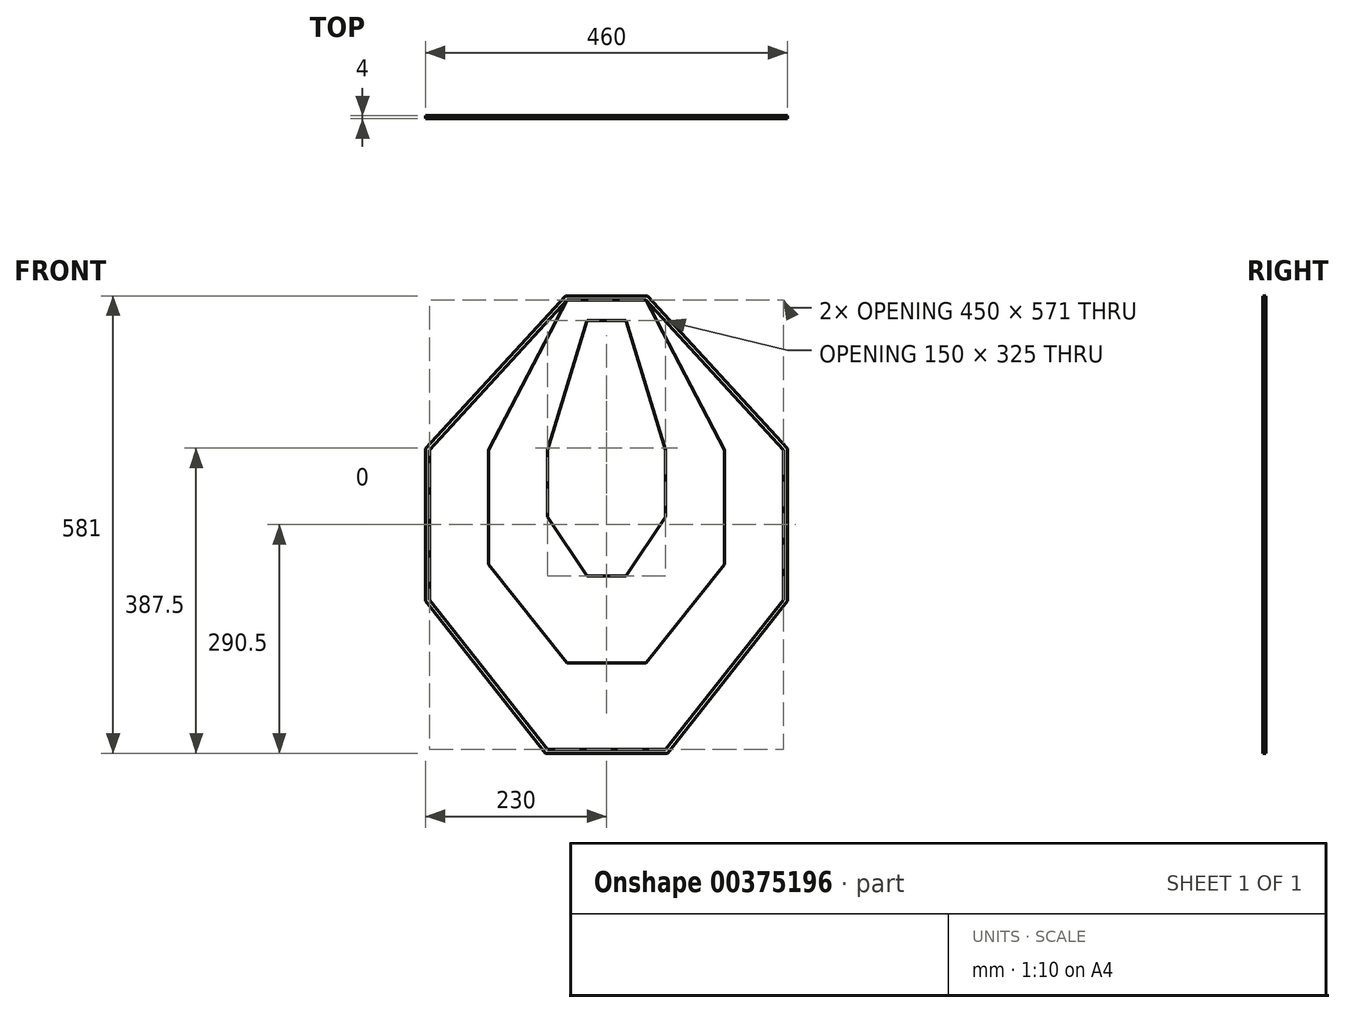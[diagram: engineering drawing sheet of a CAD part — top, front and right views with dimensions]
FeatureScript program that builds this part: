
annotation { "Feature Type Name" : "Feature", "Feature Type Description" : "" }
export const myFeature = defineFeature(function(context is Context, id is Id, definition is map)
    precondition{}
    {
        {
            var Q0;
            Q0=qCreatedBy(makeId("Front.planeOp"),FACE);
            var sketch = newSketch(context, id + "F0", { "sketchPlane" : qUnion([Q0])});
            skLineSegment(sketch, "E0", {"start": v(-25, -26) * mm, "end": v(25, -26) * mm});
            skLineSegment(sketch, "E1", {"start": v(25, -26) * mm, "end": v(75, -191) * mm});
            skLineSegment(sketch, "E2", {"start": v(75, -191) * mm, "end": v(75, -276) * mm});
            skLineSegment(sketch, "E3", {"start": v(75, -276) * mm, "end": v(25, -351) * mm});
            skLineSegment(sketch, "E4", {"start": v(25, -351) * mm, "end": v(-25, -351) * mm});
            skLineSegment(sketch, "E5", {"start": v(-25, -351) * mm, "end": v(-75, -276) * mm});
            skLineSegment(sketch, "E6", {"start": v(-75, -276) * mm, "end": v(-75, -191) * mm});
            skLineSegment(sketch, "E7", {"start": v(-75, -191) * mm, "end": v(-25, -26) * mm});
            skLineSegment(sketch, "E8", {"start": v(0, -26) * mm, "end": v(0, -191) * mm, "construction": true});
            skLineSegment(sketch, "E9", {"start": v(0, -191) * mm, "end": v(0, -351) * mm, "construction": true});
            skLineSegment(sketch, "E10", {"start": v(75, -191) * mm, "end": v(0, -191) * mm, "construction": true});
            skLineSegment(sketch, "E11", {"start": v(-75, -191) * mm, "end": v(0, -191) * mm, "construction": true});
            skLineSegment(sketch, "E12", {"start": v(0, 0) * mm, "end": v(0, -26) * mm, "construction": true});
            skSolve(sketch);
        }
        {
            var Q0;
            Q0=makeQuery(id+"F0.imprint","IMPRINT",FACE,{"disambiguationData":[TD([[makeQuery(id+"F0.imprint","IMPRINT",EDGE,{"derivedFrom":sQuery(id+"F0.wireOp",EDGE,"E0")}),-1.0]])]});
            extrude(context, id + "F1", {"entities" : qUnion([Q0]), "oppositeDirection" : true, "depth" : 3 * mm});
        }
        {
            var Q0;
            Q0=qCreatedBy(makeId("Front.planeOp"),FACE);
            var sketch = newSketch(context, id + "F2", { "sketchPlane" : qUnion([Q0])});
            skLineSegment(sketch, "E13.0", {"start": v(-75, -191) * mm, "end": v(-25, -26) * mm});
            skLineSegment(sketch, "E14.0", {"start": v(-25, -26) * mm, "end": v(25, -26) * mm});
            skLineSegment(sketch, "E15.0", {"start": v(25, -26) * mm, "end": v(75, -191) * mm});
            skLineSegment(sketch, "E16.0", {"start": v(75, -191) * mm, "end": v(75, -276) * mm});
            skLineSegment(sketch, "E17.0", {"start": v(75, -276) * mm, "end": v(25, -351) * mm});
            skLineSegment(sketch, "E18.0", {"start": v(25, -351) * mm, "end": v(-25, -351) * mm});
            skLineSegment(sketch, "E19.0", {"start": v(-25, -351) * mm, "end": v(-75, -276) * mm});
            skLineSegment(sketch, "E20.0", {"start": v(-75, -276) * mm, "end": v(-75, -191) * mm});
            skLineSegment(sketch, "E21", {"start": v(0, -191) * mm, "end": v(0, 0) * mm, "construction": true});
            skLineSegment(sketch, "E22", {"start": v(0, 0) * mm, "end": v(50, 0) * mm});
            skLineSegment(sketch, "E23", {"start": v(50, 0) * mm, "end": v(150, -191) * mm});
            skLineSegment(sketch, "E24", {"start": v(150, -191) * mm, "end": v(150, -336) * mm});
            skLineSegment(sketch, "E25", {"start": v(150, -336) * mm, "end": v(50, -461) * mm});
            skLineSegment(sketch, "E26", {"start": v(50, -461) * mm, "end": v(-50, -461) * mm});
            skLineSegment(sketch, "E27", {"start": v(-50, -461) * mm, "end": v(-150, -336) * mm});
            skLineSegment(sketch, "E28", {"start": v(-150, -336) * mm, "end": v(-150, -191) * mm});
            skLineSegment(sketch, "E29", {"start": v(-150, -191) * mm, "end": v(-50, 0) * mm});
            skLineSegment(sketch, "E30", {"start": v(-50, 0) * mm, "end": v(0, 0) * mm});
            skLineSegment(sketch, "E31", {"start": v(-150, -336) * mm, "end": v(150, -336) * mm, "construction": true});
            skLineSegment(sketch, "E32", {"start": v(0, -461) * mm, "end": v(0, -191) * mm, "construction": true});
            skLineSegment(sketch, "E33", {"start": v(150, -191) * mm, "end": v(0, -191) * mm, "construction": true});
            skLineSegment(sketch, "E34", {"start": v(-150, -191) * mm, "end": v(0, -191) * mm, "construction": true});
            skSolve(sketch);
        }
        {
            var Q0;
            Q0=makeQuery(id+"F2.imprint","IMPRINT",FACE,{"disambiguationData":[TD([[makeQuery(id+"F2.imprint","IMPRINT",EDGE,{"derivedFrom":sQuery(id+"F2.wireOp",EDGE,"E13.0")}),1.0]])]});
            extrude(context, id + "F3", {"entities" : qUnion([Q0]), "oppositeDirection" : true, "depth" : 3 * mm});
        }
        {
            var Q0;
            Q0=makeQuery(id+"F3.opExtrude","CAP_FACE",FACE,{"disambiguationData":[OSD([sQuery(id+"F2.wireOp",EDGE,"E13.0"),sQuery(id+"F2.wireOp",EDGE,"E14.0"),sQuery(id+"F2.wireOp",EDGE,"E15.0"),sQuery(id+"F2.wireOp",EDGE,"E16.0"),sQuery(id+"F2.wireOp",EDGE,"E17.0"),sQuery(id+"F2.wireOp",EDGE,"E18.0"),sQuery(id+"F2.wireOp",EDGE,"E19.0"),sQuery(id+"F2.wireOp",EDGE,"E20.0"),sQuery(id+"F2.wireOp",EDGE,"E22"),sQuery(id+"F2.wireOp",EDGE,"E23"),sQuery(id+"F2.wireOp",EDGE,"E24"),sQuery(id+"F2.wireOp",EDGE,"E25"),sQuery(id+"F2.wireOp",EDGE,"E26"),sQuery(id+"F2.wireOp",EDGE,"E27"),sQuery(id+"F2.wireOp",EDGE,"E28"),sQuery(id+"F2.wireOp",EDGE,"E29"),sQuery(id+"F2.wireOp",EDGE,"E30")])],"isStart":true});
            var sketch = newSketch(context, id + "F4", { "sketchPlane" : qUnion([Q0])});
            skLineSegment(sketch, "E35.0", {"start": v(-50, 0) * mm, "end": v(50, 0) * mm});
            skLineSegment(sketch, "E36.0", {"start": v(50, 0) * mm, "end": v(150, -191) * mm});
            skLineSegment(sketch, "E37.0", {"start": v(150, -191) * mm, "end": v(150, -336) * mm});
            skLineSegment(sketch, "E38.0", {"start": v(150, -336) * mm, "end": v(50, -461) * mm});
            skLineSegment(sketch, "E39.0", {"start": v(50, -461) * mm, "end": v(-50, -461) * mm});
            skLineSegment(sketch, "E40.0", {"start": v(-50, -461) * mm, "end": v(-150, -336) * mm});
            skLineSegment(sketch, "E41.0", {"start": v(-150, -336) * mm, "end": v(-150, -191) * mm});
            skLineSegment(sketch, "E42.0", {"start": v(-150, -191) * mm, "end": v(-50, 0) * mm});
            skLineSegment(sketch, "E43", {"start": v(50, 0) * mm, "end": v(225, -191) * mm});
            skLineSegment(sketch, "E44", {"start": v(225, -191) * mm, "end": v(225, -381) * mm});
            skLineSegment(sketch, "E45", {"start": v(225, -381) * mm, "end": v(75, -571) * mm});
            skLineSegment(sketch, "E46", {"start": v(75, -571) * mm, "end": v(-75, -571) * mm});
            skLineSegment(sketch, "E47", {"start": v(-75, -571) * mm, "end": v(-225, -381) * mm});
            skLineSegment(sketch, "E48", {"start": v(-225, -381) * mm, "end": v(-225, -191) * mm});
            skLineSegment(sketch, "E49", {"start": v(-225, -191) * mm, "end": v(-50, 0) * mm});
            skLineSegment(sketch, "E50", {"start": v(-225, -191) * mm, "end": v(-150, -191) * mm, "construction": true});
            skLineSegment(sketch, "E51", {"start": v(225, -191) * mm, "end": v(150, -191) * mm, "construction": true});
            skLineSegment(sketch, "E52", {"start": v(0, -461) * mm, "end": v(0, -571) * mm, "construction": true});
            skSolve(sketch);
        }
        {
            var Q0;
            Q0=makeQuery(id+"F4.imprint","IMPRINT",FACE,{"disambiguationData":[TD([[makeQuery(id+"F4.imprint","IMPRINT",EDGE,{"derivedFrom":sQuery(id+"F4.wireOp",EDGE,"E36.0")}),1.0]])]});
            extrude(context, id + "F5", {"entities" : qUnion([Q0]), "oppositeDirection" : true, "depth" : 3 * mm});
        }
        {
            var Q0;
            Q0=makeQuery(id+"F5.opExtrude","CAP_FACE",FACE,{"disambiguationData":[OSD([sQuery(id+"F4.wireOp",EDGE,"E36.0"),sQuery(id+"F4.wireOp",EDGE,"E37.0"),sQuery(id+"F4.wireOp",EDGE,"E38.0"),sQuery(id+"F4.wireOp",EDGE,"E39.0"),sQuery(id+"F4.wireOp",EDGE,"E40.0"),sQuery(id+"F4.wireOp",EDGE,"E41.0"),sQuery(id+"F4.wireOp",EDGE,"E42.0"),sQuery(id+"F4.wireOp",EDGE,"E43"),sQuery(id+"F4.wireOp",EDGE,"E44"),sQuery(id+"F4.wireOp",EDGE,"E45"),sQuery(id+"F4.wireOp",EDGE,"E46"),sQuery(id+"F4.wireOp",EDGE,"E47"),sQuery(id+"F4.wireOp",EDGE,"E48"),sQuery(id+"F4.wireOp",EDGE,"E49")])],"isStart":true});
            var sketch = newSketch(context, id + "F6", { "sketchPlane" : qUnion([Q0])});
            skLineSegment(sketch, "E53.0", {"start": v(-50, 0) * mm, "end": v(50, 0) * mm});
            skLineSegment(sketch, "E54.0", {"start": v(50, 0) * mm, "end": v(225, -191) * mm});
            skLineSegment(sketch, "E55.0", {"start": v(225, -191) * mm, "end": v(225, -381) * mm});
            skLineSegment(sketch, "E56.0", {"start": v(225, -381) * mm, "end": v(75, -571) * mm});
            skLineSegment(sketch, "E57.0", {"start": v(75, -571) * mm, "end": v(-75, -571) * mm});
            skLineSegment(sketch, "E58.0", {"start": v(-75, -571) * mm, "end": v(-225, -381) * mm});
            skLineSegment(sketch, "E59.0", {"start": v(-225, -191) * mm, "end": v(-50, 0) * mm});
            skLineSegment(sketch, "E60.0", {"start": v(-225, -381) * mm, "end": v(-225, -191) * mm});
            skLineSegment(sketch, "E61.0", {"start": v(-52.2, 5) * mm, "end": v(52.2, 5) * mm});
            skLineSegment(sketch, "E61.1", {"start": v(-230, -189.06) * mm, "end": v(-52.2, 5) * mm});
            skLineSegment(sketch, "E61.2", {"start": v(52.2, 5) * mm, "end": v(230, -189.06) * mm});
            skLineSegment(sketch, "E61.3", {"start": v(-230, -382.74) * mm, "end": v(-230, -189.06) * mm});
            skLineSegment(sketch, "E61.4", {"start": v(230, -189.06) * mm, "end": v(230, -382.74) * mm});
            skLineSegment(sketch, "E61.5", {"start": v(230, -382.74) * mm, "end": v(77.42, -576) * mm});
            skLineSegment(sketch, "E61.6", {"start": v(77.42, -576) * mm, "end": v(-77.42, -576) * mm});
            skLineSegment(sketch, "E61.7", {"start": v(-77.42, -576) * mm, "end": v(-230, -382.74) * mm});
            skSolve(sketch);
        }
        {
            var Q0;
            Q0=makeQuery(id+"F6.imprint","IMPRINT",FACE,{"disambiguationData":[TD([[makeQuery(id+"F6.imprint","IMPRINT",EDGE,{"derivedFrom":sQuery(id+"F6.wireOp",EDGE,"E53.0")}),1.0]])]});
            extrude(context, id + "F7", {"entities" : qUnion([Q0]), "oppositeDirection" : true, "depth" : 3 * mm});
        }
        {
            var Q0;
            Q0=makeQuery(id+"F5.opExtrude","CAP_FACE",FACE,{"disambiguationData":[OSD([sQuery(id+"F4.wireOp",EDGE,"E36.0"),sQuery(id+"F4.wireOp",EDGE,"E37.0"),sQuery(id+"F4.wireOp",EDGE,"E38.0"),sQuery(id+"F4.wireOp",EDGE,"E39.0"),sQuery(id+"F4.wireOp",EDGE,"E40.0"),sQuery(id+"F4.wireOp",EDGE,"E41.0"),sQuery(id+"F4.wireOp",EDGE,"E42.0"),sQuery(id+"F4.wireOp",EDGE,"E43"),sQuery(id+"F4.wireOp",EDGE,"E44"),sQuery(id+"F4.wireOp",EDGE,"E45"),sQuery(id+"F4.wireOp",EDGE,"E46"),sQuery(id+"F4.wireOp",EDGE,"E47"),sQuery(id+"F4.wireOp",EDGE,"E48"),sQuery(id+"F4.wireOp",EDGE,"E49")])],"isStart":false});
            var sketch = newSketch(context, id + "F8", { "sketchPlane" : qUnion([Q0])});
            skLineSegment(sketch, "E62.0", {"start": v(225, -191) * mm, "end": v(50, 0) * mm});
            skLineSegment(sketch, "E63.0", {"start": v(50, 0) * mm, "end": v(-50, 0) * mm});
            skLineSegment(sketch, "E64.0", {"start": v(75, -571) * mm, "end": v(225, -381) * mm});
            skLineSegment(sketch, "E65.0", {"start": v(225, -381) * mm, "end": v(225, -191) * mm});
            skLineSegment(sketch, "E66.0", {"start": v(-75, -571) * mm, "end": v(75, -571) * mm});
            skLineSegment(sketch, "E67.0", {"start": v(-225, -381) * mm, "end": v(-75, -571) * mm});
            skLineSegment(sketch, "E68.0", {"start": v(-50, 0) * mm, "end": v(-225, -191) * mm});
            skLineSegment(sketch, "E69.0", {"start": v(-225, -191) * mm, "end": v(-225, -381) * mm});
            skSolve(sketch);
        }
        {
            var Q0;
            Q0 = qSketchRegion(id + "F8", true);
            extrude(context, id + "F9", {"entities" : qUnion([Q0]), "depth" : 1 * mm});
        }
        {
            var Q0;
            Q0=makeQuery(id+"F7.opExtrude","CAP_FACE",FACE,{"disambiguationData":[OSD([sQuery(id+"F6.wireOp",EDGE,"E53.0"),sQuery(id+"F6.wireOp",EDGE,"E54.0"),sQuery(id+"F6.wireOp",EDGE,"E55.0"),sQuery(id+"F6.wireOp",EDGE,"E56.0"),sQuery(id+"F6.wireOp",EDGE,"E57.0"),sQuery(id+"F6.wireOp",EDGE,"E58.0"),sQuery(id+"F6.wireOp",EDGE,"E59.0"),sQuery(id+"F6.wireOp",EDGE,"E60.0"),sQuery(id+"F6.wireOp",EDGE,"E61.0"),sQuery(id+"F6.wireOp",EDGE,"E61.1"),sQuery(id+"F6.wireOp",EDGE,"E61.2"),sQuery(id+"F6.wireOp",EDGE,"E61.3"),sQuery(id+"F6.wireOp",EDGE,"E61.4"),sQuery(id+"F6.wireOp",EDGE,"E61.5"),sQuery(id+"F6.wireOp",EDGE,"E61.6"),sQuery(id+"F6.wireOp",EDGE,"E61.7")])],"isStart":false});
            var sketch = newSketch(context, id + "F10", { "sketchPlane" : qUnion([Q0])});
            skLineSegment(sketch, "E70.0", {"start": v(50, 0) * mm, "end": v(-50, 0) * mm});
            skLineSegment(sketch, "E71.0", {"start": v(52.2, 5) * mm, "end": v(-52.2, 5) * mm});
            skLineSegment(sketch, "E72.0", {"start": v(230, -189.06) * mm, "end": v(52.2, 5) * mm});
            skLineSegment(sketch, "E73.0", {"start": v(225, -191) * mm, "end": v(50, 0) * mm});
            skLineSegment(sketch, "E74.0", {"start": v(225, -381) * mm, "end": v(225, -191) * mm});
            skLineSegment(sketch, "E75.0", {"start": v(230, -382.74) * mm, "end": v(230, -189.06) * mm});
            skLineSegment(sketch, "E76.0", {"start": v(77.42, -576) * mm, "end": v(230, -382.74) * mm});
            skLineSegment(sketch, "E77.0", {"start": v(75, -571) * mm, "end": v(225, -381) * mm});
            skLineSegment(sketch, "E78.0", {"start": v(-75, -571) * mm, "end": v(75, -571) * mm});
            skLineSegment(sketch, "E79.0", {"start": v(-225, -381) * mm, "end": v(-75, -571) * mm});
            skLineSegment(sketch, "E80.0", {"start": v(-230, -382.74) * mm, "end": v(-77.42, -576) * mm});
            skLineSegment(sketch, "E81.0", {"start": v(-77.42, -576) * mm, "end": v(77.42, -576) * mm});
            skLineSegment(sketch, "E82.0", {"start": v(-50, 0) * mm, "end": v(-225, -191) * mm});
            skLineSegment(sketch, "E83.0", {"start": v(-225, -191) * mm, "end": v(-225, -381) * mm});
            skLineSegment(sketch, "E84.0", {"start": v(-230, -189.06) * mm, "end": v(-230, -382.74) * mm});
            skLineSegment(sketch, "E85.0", {"start": v(-52.2, 5) * mm, "end": v(-230, -189.06) * mm});
            skSolve(sketch);
        }
        {
            var Q0;
            Q0=makeQuery(id+"F10.imprint","IMPRINT",FACE,{"disambiguationData":[TD([[makeQuery(id+"F10.imprint","IMPRINT",EDGE,{"derivedFrom":sQuery(id+"F10.wireOp",EDGE,"E70.0")}),-1.0]])]});
            extrude(context, id + "F11", {"entities" : qUnion([Q0]), "depth" : 1 * mm});
        }
    });
